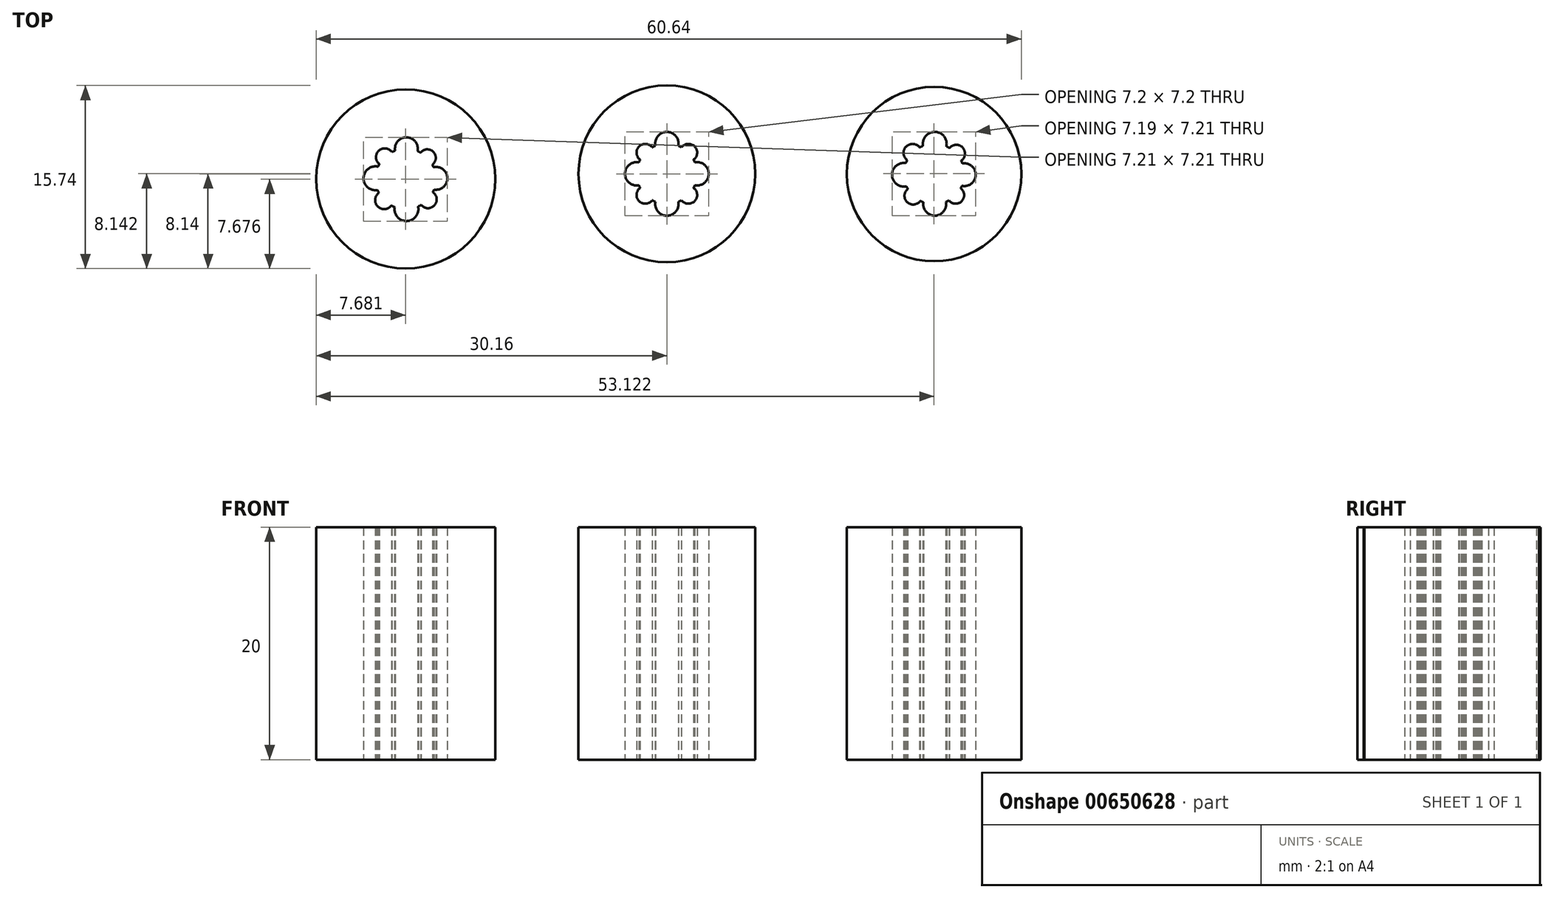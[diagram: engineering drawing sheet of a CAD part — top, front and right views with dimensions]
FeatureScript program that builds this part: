
annotation { "Feature Type Name" : "Feature", "Feature Type Description" : "" }
export const myFeature = defineFeature(function(context is Context, id is Id, definition is map)
    precondition{}
    {
        {
            var Q0;
            Q0=qCreatedBy(makeId("Top.planeOp"),FACE);
            var sketch = newSketch(context, id + "F0", { "sketchPlane" : qUnion([Q0])});
            skCircle(sketch, "E0", {"center": v(0, 0) * mm, "radius": 7.6 * mm});
            skCircle(sketch, "E1", {"center": v(22.98, -0.02) * mm, "radius": 7.5 * mm});
            skCircle(sketch, "E2", {"center": v(-22.46, -0.44) * mm, "radius": 7.7 * mm});
            skArc(sketch, "E3", {"start": v(2.4, 0.98) * mm, "mid": v(2.36, 1.1) * mm, "end": v(2.3, 1.21) * mm});
            skArc(sketch, "E4", {"start": v(2.4, -0.98) * mm, "mid": v(3.6, 0) * mm, "end": v(2.4, 0.98) * mm});
            skArc(sketch, "E5", {"start": v(-0.98, -2.4) * mm, "mid": v(0, -3.6) * mm, "end": v(0.98, -2.4) * mm});
            skArc(sketch, "E6", {"start": v(1.26, -2.27) * mm, "mid": v(2.4, -2.35) * mm, "end": v(2.3, -1.21) * mm});
            skArc(sketch, "E7.MirrorC", {"start": v(-1.26, -2.27) * mm, "mid": v(-2.4, -2.35) * mm, "end": v(-2.3, -1.21) * mm});
            skArc(sketch, "E8.MirrorC", {"start": v(-2.4, -0.98) * mm, "mid": v(-3.6, 0) * mm, "end": v(-2.4, 0.98) * mm});
            skArc(sketch, "E9.MirrorC", {"start": v(1.26, 2.27) * mm, "mid": v(2.4, 2.35) * mm, "end": v(2.3, 1.21) * mm});
            skArc(sketch, "E10.MirrorC", {"start": v(-0.98, 2.4) * mm, "mid": v(0, 3.6) * mm, "end": v(0.98, 2.4) * mm});
            skArc(sketch, "E11.MirrorC", {"start": v(-1.26, 2.27) * mm, "mid": v(-2.4, 2.35) * mm, "end": v(-2.3, 1.21) * mm});
            skArc(sketch, "E12.trimOffspring", {"start": v(2.3, -1.21) * mm, "mid": v(2.36, -1.1) * mm, "end": v(2.4, -0.98) * mm});
            skArc(sketch, "E13.trimOffspring", {"start": v(0.98, -2.4) * mm, "mid": v(1.12, -2.35) * mm, "end": v(1.26, -2.27) * mm});
            skArc(sketch, "E14.trimOffspring", {"start": v(-1.26, -2.27) * mm, "mid": v(-1.12, -2.35) * mm, "end": v(-0.98, -2.4) * mm});
            skArc(sketch, "E15.trimOffspring", {"start": v(-2.4, -0.98) * mm, "mid": v(-2.36, -1.1) * mm, "end": v(-2.3, -1.21) * mm});
            skArc(sketch, "E16.trimOffspring", {"start": v(-2.3, 1.21) * mm, "mid": v(-2.36, 1.1) * mm, "end": v(-2.4, 0.98) * mm});
            skArc(sketch, "E17.trimOffspring", {"start": v(-0.98, 2.4) * mm, "mid": v(-1.12, 2.35) * mm, "end": v(-1.26, 2.27) * mm});
            skArc(sketch, "E18.trimOffspring", {"start": v(1.26, 2.27) * mm, "mid": v(1.12, 2.35) * mm, "end": v(0.98, 2.4) * mm});
            skArc(sketch, "E19", {"start": v(25.42, 0.89) * mm, "mid": v(25.37, 1) * mm, "end": v(25.32, 1.13) * mm});
            skArc(sketch, "E20", {"start": v(25.38, -1.03) * mm, "mid": v(26.56, -0.1) * mm, "end": v(25.42, 0.89) * mm});
            skArc(sketch, "E21", {"start": v(22.07, -2.45) * mm, "mid": v(23.06, -3.6) * mm, "end": v(24, -2.41) * mm});
            skArc(sketch, "E22", {"start": v(24.26, -2.28) * mm, "mid": v(25.36, -2.35) * mm, "end": v(25.27, -1.25) * mm});
            skArc(sketch, "E23.MirrorC", {"start": v(21.79, -2.33) * mm, "mid": v(20.66, -2.43) * mm, "end": v(20.72, -1.3) * mm});
            skArc(sketch, "E24.MirrorC", {"start": v(20.6, -1.07) * mm, "mid": v(19.37, -0.1) * mm, "end": v(20.56, 0.92) * mm});
            skArc(sketch, "E25.MirrorC", {"start": v(24.31, 2.21) * mm, "mid": v(25.44, 2.25) * mm, "end": v(25.32, 1.13) * mm});
            skArc(sketch, "E26.MirrorC", {"start": v(22.03, 2.4) * mm, "mid": v(23.06, 3.6) * mm, "end": v(24.04, 2.36) * mm});
            skArc(sketch, "E27.MirrorC", {"start": v(21.74, 2.27) * mm, "mid": v(20.57, 2.34) * mm, "end": v(20.67, 1.17) * mm});
            skArc(sketch, "E28.trimOffspring", {"start": v(25.27, -1.25) * mm, "mid": v(25.33, -1.14) * mm, "end": v(25.38, -1.03) * mm});
            skArc(sketch, "E29.trimOffspring", {"start": v(24, -2.41) * mm, "mid": v(24.13, -2.35) * mm, "end": v(24.26, -2.28) * mm});
            skArc(sketch, "E30.trimOffspring", {"start": v(21.79, -2.33) * mm, "mid": v(21.93, -2.4) * mm, "end": v(22.07, -2.45) * mm});
            skArc(sketch, "E31.trimOffspring", {"start": v(20.6, -1.07) * mm, "mid": v(20.66, -1.19) * mm, "end": v(20.72, -1.3) * mm});
            skArc(sketch, "E32.trimOffspring", {"start": v(20.67, 1.17) * mm, "mid": v(20.61, 1.05) * mm, "end": v(20.56, 0.92) * mm});
            skArc(sketch, "E33.trimOffspring", {"start": v(22.03, 2.4) * mm, "mid": v(21.88, 2.34) * mm, "end": v(21.74, 2.27) * mm});
            skArc(sketch, "E34.trimOffspring", {"start": v(24.31, 2.21) * mm, "mid": v(24.18, 2.29) * mm, "end": v(24.04, 2.36) * mm});
            skArc(sketch, "E35", {"start": v(-20.06, 0.57) * mm, "mid": v(-20.11, 0.68) * mm, "end": v(-20.17, 0.79) * mm});
            skArc(sketch, "E36", {"start": v(-20.02, -1.36) * mm, "mid": v(-18.87, -0.37) * mm, "end": v(-20.06, 0.57) * mm});
            skArc(sketch, "E37", {"start": v(-23.4, -2.86) * mm, "mid": v(-22.37, -4.07) * mm, "end": v(-21.4, -2.82) * mm});
            skArc(sketch, "E38", {"start": v(-21.13, -2.68) * mm, "mid": v(-19.99, -2.71) * mm, "end": v(-20.12, -1.58) * mm});
            skArc(sketch, "E39.MirrorC", {"start": v(-23.7, -2.73) * mm, "mid": v(-24.86, -2.8) * mm, "end": v(-24.76, -1.64) * mm});
            skArc(sketch, "E40.MirrorC", {"start": v(-24.87, -1.4) * mm, "mid": v(-26.08, -0.37) * mm, "end": v(-24.83, 0.62) * mm});
            skArc(sketch, "E41.MirrorC", {"start": v(-21.17, 1.82) * mm, "mid": v(-20.08, 1.88) * mm, "end": v(-20.17, 0.79) * mm});
            skArc(sketch, "E42.MirrorC", {"start": v(-23.37, 2) * mm, "mid": v(-22.37, 3.14) * mm, "end": v(-21.43, 1.95) * mm});
            skArc(sketch, "E43.MirrorC", {"start": v(-23.64, 1.87) * mm, "mid": v(-24.78, 1.98) * mm, "end": v(-24.72, 0.84) * mm});
            skArc(sketch, "E44.trimOffspring", {"start": v(-20.12, -1.58) * mm, "mid": v(-20.07, -1.47) * mm, "end": v(-20.02, -1.36) * mm});
            skArc(sketch, "E45.trimOffspring", {"start": v(-21.4, -2.82) * mm, "mid": v(-21.26, -2.75) * mm, "end": v(-21.13, -2.68) * mm});
            skArc(sketch, "E46.trimOffspring", {"start": v(-23.7, -2.73) * mm, "mid": v(-23.55, -2.8) * mm, "end": v(-23.4, -2.86) * mm});
            skArc(sketch, "E47.trimOffspring", {"start": v(-24.87, -1.4) * mm, "mid": v(-24.82, -1.52) * mm, "end": v(-24.76, -1.64) * mm});
            skArc(sketch, "E48.trimOffspring", {"start": v(-24.72, 0.84) * mm, "mid": v(-24.78, 0.73) * mm, "end": v(-24.83, 0.62) * mm});
            skArc(sketch, "E49.trimOffspring", {"start": v(-23.37, 2) * mm, "mid": v(-23.5, 1.94) * mm, "end": v(-23.64, 1.87) * mm});
            skArc(sketch, "E50.trimOffspring", {"start": v(-21.17, 1.82) * mm, "mid": v(-21.3, 1.89) * mm, "end": v(-21.43, 1.95) * mm});
            skSolve(sketch);
        }
        {
            var Q0;
            Q0 = qSketchRegion(id + "F0", true);
            extrude(context, id + "F1", {"entities" : qUnion([Q0]), "depth" : 20 * mm, "offsetDistance" : 25 * mm});
        }
    });
